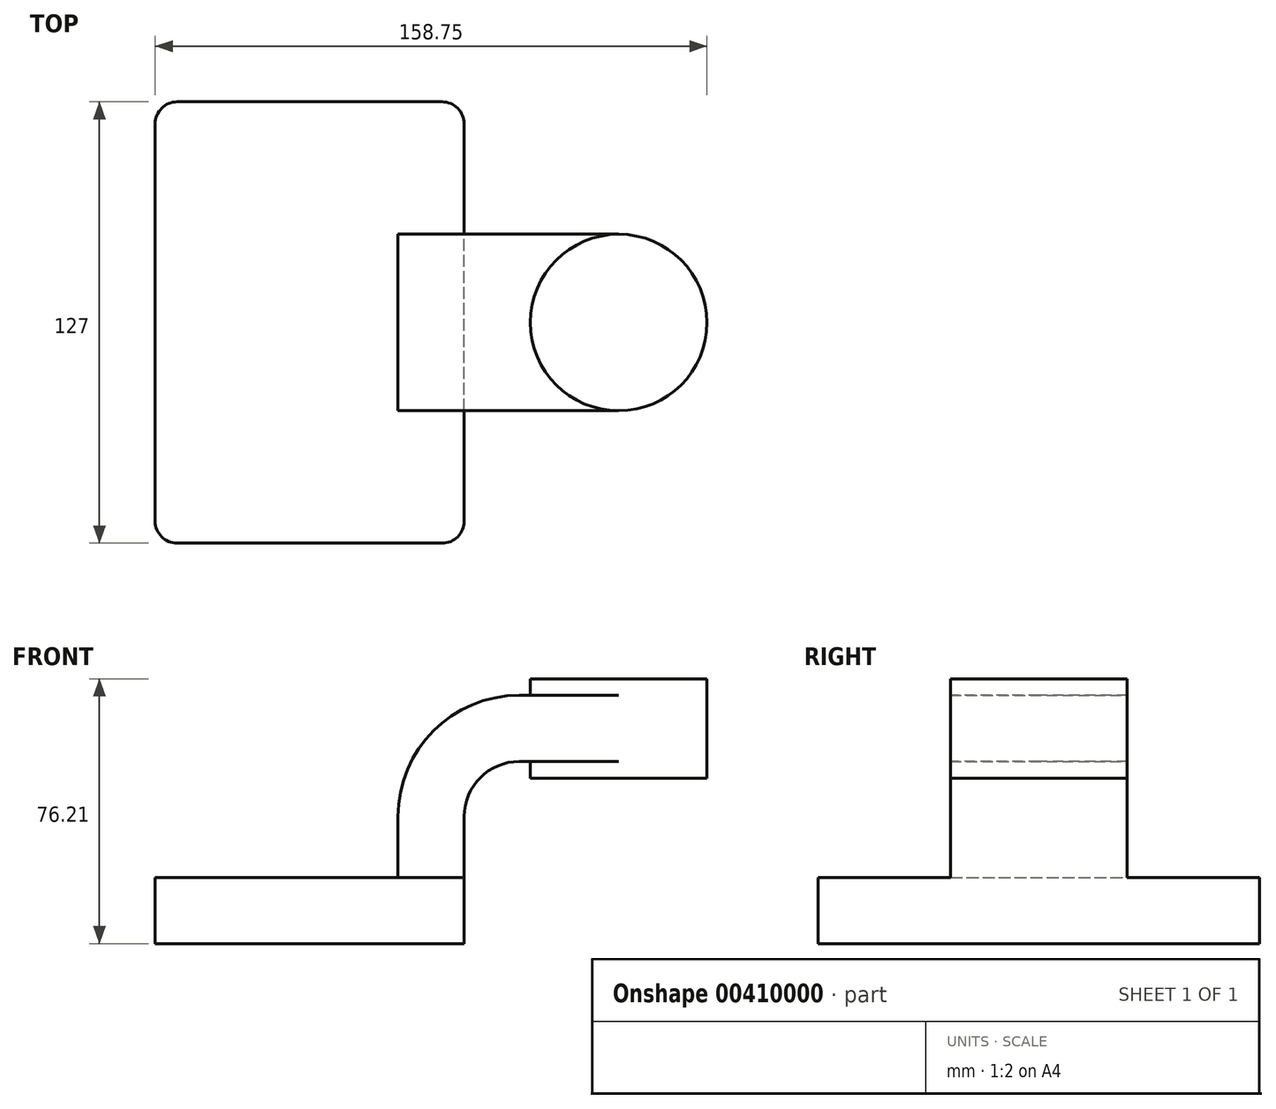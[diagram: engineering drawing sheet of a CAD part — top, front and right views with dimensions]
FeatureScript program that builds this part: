
annotation { "Feature Type Name" : "Feature", "Feature Type Description" : "" }
export const myFeature = defineFeature(function(context is Context, id is Id, definition is map)
    precondition{}
    {
        {
            var Q0;
            Q0=qCreatedBy(makeId("Front.planeOp"),FACE);
            var sketch = newSketch(context, id + "F0", { "sketchPlane" : qUnion([Q0])});
            skLineSegment(sketch, "E0.bottom", {"start": v(-44.45, -9.52) * mm, "end": v(44.45, -9.52) * mm});
            skLineSegment(sketch, "E0.top", {"start": v(-44.45, 9.53) * mm, "end": v(44.45, 9.53) * mm});
            skLineSegment(sketch, "E0.left", {"start": v(-44.45, -9.52) * mm, "end": v(-44.45, 9.53) * mm});
            skLineSegment(sketch, "E0.right", {"start": v(44.45, -9.52) * mm, "end": v(44.45, 9.53) * mm});
            skPoint(sketch, "E0.middle", {"position": v(0, 0) * mm});
            skLineSegment(sketch, "E1.bottom", {"start": v(63.5, 38.1) * mm, "end": v(114.3, 38.1) * mm});
            skLineSegment(sketch, "E1.top", {"start": v(63.5, 66.68) * mm, "end": v(114.3, 66.68) * mm});
            skLineSegment(sketch, "E1.left", {"start": v(63.5, 38.1) * mm, "end": v(63.5, 66.68) * mm});
            skLineSegment(sketch, "E1.right", {"start": v(114.3, 38.1) * mm, "end": v(114.3, 66.68) * mm});
            skPoint(sketch, "E1.middle", {"position": v(88.9, 52.39) * mm});
            skLineSegment(sketch, "E2", {"start": v(44.45, 9.53) * mm, "end": v(44.45, 27) * mm});
            skArc(sketch, "E3", {"start": v(44.45, 27) * mm, "mid": v(49.1, 38.23) * mm, "end": v(60.32, 42.88) * mm});
            skLineSegment(sketch, "E4", {"start": v(60.32, 42.88) * mm, "end": v(88.9, 42.88) * mm});
            skLineSegment(sketch, "E5.0", {"start": v(60.32, 61.93) * mm, "end": v(88.9, 61.93) * mm});
            skArc(sketch, "E5.1", {"start": v(25.4, 27) * mm, "mid": v(35.63, 51.7) * mm, "end": v(60.32, 61.93) * mm});
            skLineSegment(sketch, "E5.2", {"start": v(25.4, 9.53) * mm, "end": v(25.4, 27) * mm});
            skFitSpline(sketch, "E6", {"points": [v(-44.45, 9.53) * mm, v(60.33, 61.93) * mm], "startDerivative": vector(93.55, 80.6) * mm, "endDerivative": vector(214.4, -21.65) * mm});
            skLineSegment(sketch, "E7", {"start": v(88.9, 38.1) * mm, "end": v(88.9, 66.68) * mm});
            skPoint(sketch, "E7.endSnap0", {"position": v(88.9, 66.68) * mm});
            skSolve(sketch);
        }
        {
            var Q0;
            Q0=makeQuery(id+"F0.imprint","IMPRINT",FACE,{"disambiguationData":[TD([[makeQuery(id+"F0.imprint","IMPRINT",EDGE,{"derivedFrom":sQuery(id+"F0.wireOp",EDGE,"E0.bottom")}),1.0]])]});
            extrude(context, id + "F1", {"entities" : qUnion([Q0]), "endBound" : BoundingType.SYMMETRIC, "depth" : 127 * mm});
        }
        {
            var Q0;
            {var subQ0=sQuery(id+"F0.wireOp",EDGE,"E2");Q0=makeQuery(id+"F0.imprint","IMPRINT",FACE,{"disambiguationData":[TD([[makeQuery(id+"F0.imprint","IMPRINT",EDGE,{"derivedFrom":subQ0}),1.0]])]});}
            var Q1;
            {var subQ0=sQuery(id+"F0.wireOp",EDGE,"E4");var subQ1=sQuery(id+"F0.wireOp",EDGE,"E1.left");var subQ2=makeQuery(id+"F0.imprint","INTERSECT",VERTEX,{"derivedFrom":[subQ1,subQ0]});Q1=makeQuery(id+"F0.imprint","IMPRINT",FACE,{"disambiguationData":[TD([[makeQuery(id+"F0.imprint","IMPRINT",EDGE,{"disambiguationData":[TD([[subQ2,-1.0]])],"derivedFrom":subQ1}),-1.0]])]});}
            extrude(context, id + "F2", {"entities" : qUnion([Q0, Q1]), "operationType" : NewBodyOperationType.ADD, "endBound" : BoundingType.SYMMETRIC, "depth" : 50.8 * mm});
        }
        {
            var Q0;
            Q0=makeQuery(id+"F0.imprint","IMPRINT",FACE,{"disambiguationData":[TD([[makeQuery(id+"F0.imprint","IMPRINT",EDGE,{"derivedFrom":sQuery(id+"F0.wireOp",EDGE,"E5.1")}),1.0]])]});
            extrude(context, id + "F3", {"entities" : qUnion([Q0]), "operationType" : NewBodyOperationType.ADD, "endBound" : BoundingType.SYMMETRIC, "depth" : 15.88 * mm});
        }
        {
            var Q0;
            {var subQ4=sQuery(id+"F0.wireOp",EDGE,"E1.right");Q0=makeQuery(id+"F0.imprint","IMPRINT",FACE,{"disambiguationData":[TD([[makeQuery(id+"F0.imprint","IMPRINT",EDGE,{"derivedFrom":subQ4}),1.0]])]});}
            var Q1;
            Q1=sQuery(id+"F0.wireOp",EDGE,"E7");
            revolve(context, id + "F4", {"operationType" : NewBodyOperationType.ADD, "entities" : qUnion([Q0]), "axis" : qUnion([Q1]), "revolveType" : RevolveType.FULL});
        }
        {
            var Q0;
            Q0=makeQuery(id+"F1.opExtrude","CAP_EDGE",EDGE,{"disambiguationData":[OSD([sQuery(id+"F0.wireOp",EDGE,"E0.left")])],"isStart":false});
            var Q1;
            Q1=makeQuery(id+"F1.opExtrude","CAP_EDGE",EDGE,{"disambiguationData":[OSD([sQuery(id+"F0.wireOp",EDGE,"E0.right")])],"isStart":false});
            var Q2;
            Q2=makeQuery(id+"F1.opExtrude","CAP_EDGE",EDGE,{"disambiguationData":[OSD([sQuery(id+"F0.wireOp",EDGE,"E0.right")])],"isStart":true});
            var Q3;
            Q3=makeQuery(id+"F1.opExtrude","CAP_EDGE",EDGE,{"disambiguationData":[OSD([sQuery(id+"F0.wireOp",EDGE,"E0.left")])],"isStart":true});
            fillet(context, id + "F5", {"entities" : qUnion([Q0, Q1, Q2, Q3]), "radius" : 6.35 * mm, "tangentPropagation" : true, "allowEdgeOverflow" : false});
        }
    });
